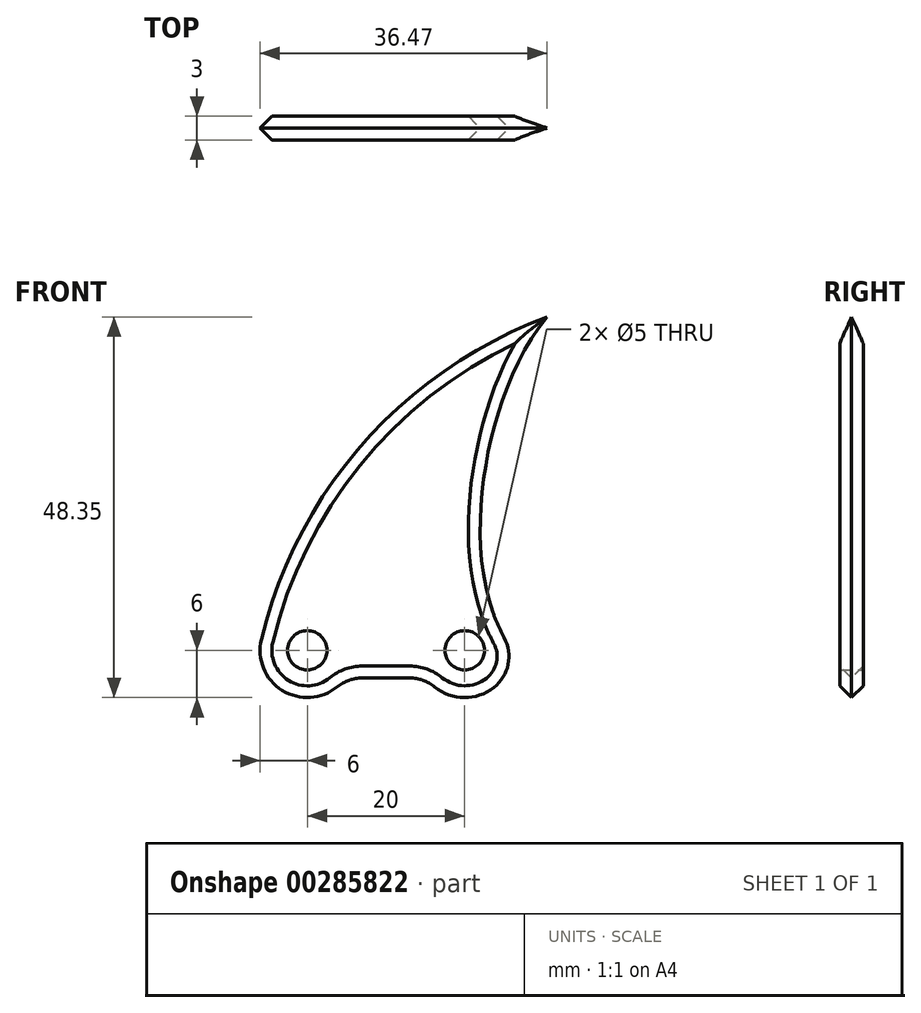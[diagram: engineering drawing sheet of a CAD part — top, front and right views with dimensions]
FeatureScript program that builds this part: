
annotation { "Feature Type Name" : "Feature", "Feature Type Description" : "" }
export const myFeature = defineFeature(function(context is Context, id is Id, definition is map)
    precondition{}
    {
        {
            var Q0;
            Q0=qCreatedBy(makeId("Front.planeOp"),FACE);
            var sketch = newSketch(context, id + "F0", { "sketchPlane" : qUnion([Q0])});
            skLineSegment(sketch, "E0.bottom", {"start": v(10, 3.5) * mm, "end": v(-10, 3.5) * mm});
            skLineSegment(sketch, "E0.top", {"start": v(10, -3.5) * mm, "end": v(-10, -3.5) * mm});
            skLineSegment(sketch, "E0.left", {"start": v(10, 3.5) * mm, "end": v(10, -3.5) * mm});
            skLineSegment(sketch, "E0.right", {"start": v(-10, 3.5) * mm, "end": v(-10, -3.5) * mm});
            skPoint(sketch, "E0.middle", {"position": v(0, 0) * mm});
            skCircle(sketch, "E1", {"center": v(-10, 0) * mm, "radius": 6 * mm});
            skCircle(sketch, "E2", {"center": v(10, 0) * mm, "radius": 6 * mm});
            skCircle(sketch, "E3", {"center": v(-10, 0) * mm, "radius": 2.5 * mm});
            skCircle(sketch, "E4", {"center": v(10, 0) * mm, "radius": 2.5 * mm});
            skCircle(sketch, "E5", {"center": v(40.77, -12.21) * mm, "radius": 58.21 * mm});
            skFitSpline(sketch, "E6", {"points": [v(20.47, 42.35) * mm, v(16, 0) * mm], "startDerivative": vector(-22.46, -26.22) * mm, "endDerivative": vector(23.71, -34.09) * mm});
            skSolve(sketch);
        }
        {
            var Q0;
            {var subQ2=sQuery(id+"F0.wireOp",EDGE,"E0.bottom");var subQ4=sQuery(id+"F0.wireOp",EDGE,"E1");var subQ5=makeQuery(id+"F0.imprint","INTERSECT",VERTEX,{"derivedFrom":[subQ2,subQ4]});Q0=makeQuery(id+"F0.imprint","IMPRINT",FACE,{"disambiguationData":[TD([[makeQuery(id+"F0.imprint","IMPRINT",EDGE,{"disambiguationData":[TD([[subQ5,-1.0]])],"derivedFrom":subQ4}),1.0]])]});}
            var Q1;
            {var subQ0=sQuery(id+"F0.wireOp",EDGE,"E2");var subQ1=sQuery(id+"F0.wireOp",EDGE,"E0.bottom");var subQ2=makeQuery(id+"F0.imprint","INTERSECT",VERTEX,{"derivedFrom":[subQ1,subQ0]});Q1=makeQuery(id+"F0.imprint","IMPRINT",FACE,{"disambiguationData":[TD([[makeQuery(id+"F0.imprint","IMPRINT",EDGE,{"disambiguationData":[TD([[subQ2,-1.0]])],"derivedFrom":subQ1}),1.0]])]});}
            var Q2;
            {var subQ2=sQuery(id+"F0.wireOp",EDGE,"E0.bottom");var subQ4=sQuery(id+"F0.wireOp",EDGE,"E1");var subQ5=makeQuery(id+"F0.imprint","INTERSECT",VERTEX,{"derivedFrom":[subQ2,subQ4]});Q2=makeQuery(id+"F0.imprint","IMPRINT",FACE,{"disambiguationData":[TD([[makeQuery(id+"F0.imprint","IMPRINT",EDGE,{"disambiguationData":[TD([[subQ5,1.0]])],"derivedFrom":subQ4}),1.0]])]});}
            var Q3;
            {var subQ2=sQuery(id+"F0.wireOp",EDGE,"E0.bottom");var subQ4=sQuery(id+"F0.wireOp",EDGE,"E2");var subQ5=makeQuery(id+"F0.imprint","INTERSECT",VERTEX,{"derivedFrom":[subQ2,subQ4]});Q3=makeQuery(id+"F0.imprint","IMPRINT",FACE,{"disambiguationData":[TD([[makeQuery(id+"F0.imprint","IMPRINT",EDGE,{"disambiguationData":[TD([[subQ5,-1.0]])],"derivedFrom":subQ4}),1.0]])]});}
            var Q4;
            {var subQ2=sQuery(id+"F0.wireOp",EDGE,"E0.bottom");var subQ4=sQuery(id+"F0.wireOp",EDGE,"E2");var subQ5=makeQuery(id+"F0.imprint","INTERSECT",VERTEX,{"derivedFrom":[subQ2,subQ4]});Q4=makeQuery(id+"F0.imprint","IMPRINT",FACE,{"disambiguationData":[TD([[makeQuery(id+"F0.imprint","IMPRINT",EDGE,{"disambiguationData":[TD([[subQ5,1.0]])],"derivedFrom":subQ4}),1.0]])]});}
            var Q5;
            {var subQ5=sQuery(id+"F0.wireOp",EDGE,"E0.bottom");var subQ7=sQuery(id+"F0.wireOp",EDGE,"E2");var subQ8=makeQuery(id+"F0.imprint","INTERSECT",VERTEX,{"derivedFrom":[subQ5,subQ7]});Q5=makeQuery(id+"F0.imprint","IMPRINT",FACE,{"disambiguationData":[TD([[makeQuery(id+"F0.imprint","IMPRINT",EDGE,{"disambiguationData":[TD([[subQ8,-1.0]])],"derivedFrom":subQ5}),-1.0]])]});}
            extrude(context, id + "F1", {"entities" : qUnion([Q0, Q1, Q2, Q3, Q4, Q5]), "endBound" : BoundingType.SYMMETRIC, "depth" : 3 * mm});
        }
        {
            var Q0;
            Q0=makeQuery(id+"F1.opExtrude","SWEPT_EDGE",EDGE,{"disambiguationData":[OSD([sQuery(id+"F0.wireOp",EDGE,"E0.bottom"),sQuery(id+"F0.wireOp",EDGE,"E1")])]});
            var Q1;
            Q1=makeQuery(id+"F1.opExtrude","SWEPT_EDGE",EDGE,{"disambiguationData":[OSD([sQuery(id+"F0.wireOp",EDGE,"E0.bottom"),sQuery(id+"F0.wireOp",EDGE,"E2")])]});
            var Q2;
            Q2=makeQuery(id+"F1.opExtrude","SWEPT_EDGE",EDGE,{"disambiguationData":[OSD([sQuery(id+"F0.wireOp",EDGE,"E0.top"),sQuery(id+"F0.wireOp",EDGE,"E1")])]});
            var Q3;
            Q3=makeQuery(id+"F1.opExtrude","SWEPT_EDGE",EDGE,{"disambiguationData":[OSD([sQuery(id+"F0.wireOp",EDGE,"E0.top"),sQuery(id+"F0.wireOp",EDGE,"E2")])]});
            fillet(context, id + "F2", {"entities" : qUnion([Q0, Q1, Q2, Q3]), "radius" : 5 * mm, "tangentPropagation" : true, "allowEdgeOverflow" : false});
        }
        {
            var Q0;
            Q0=makeQuery(id+"F1.opExtrude","CAP_EDGE",EDGE,{"disambiguationData":[OSD([sQuery(id+"F0.wireOp",EDGE,"E6")])],"isStart":false});
            var Q1;
            Q1=makeQuery(id+"F1.opExtrude","CAP_EDGE",EDGE,{"disambiguationData":[OSD([sQuery(id+"F0.wireOp",EDGE,"E6")])],"isStart":true});
            chamfer(context, id + "F3", {"entities" : qUnion([Q0, Q1]), "width" : 1.5 * mm, "tangentPropagation" : true});
        }
    });
